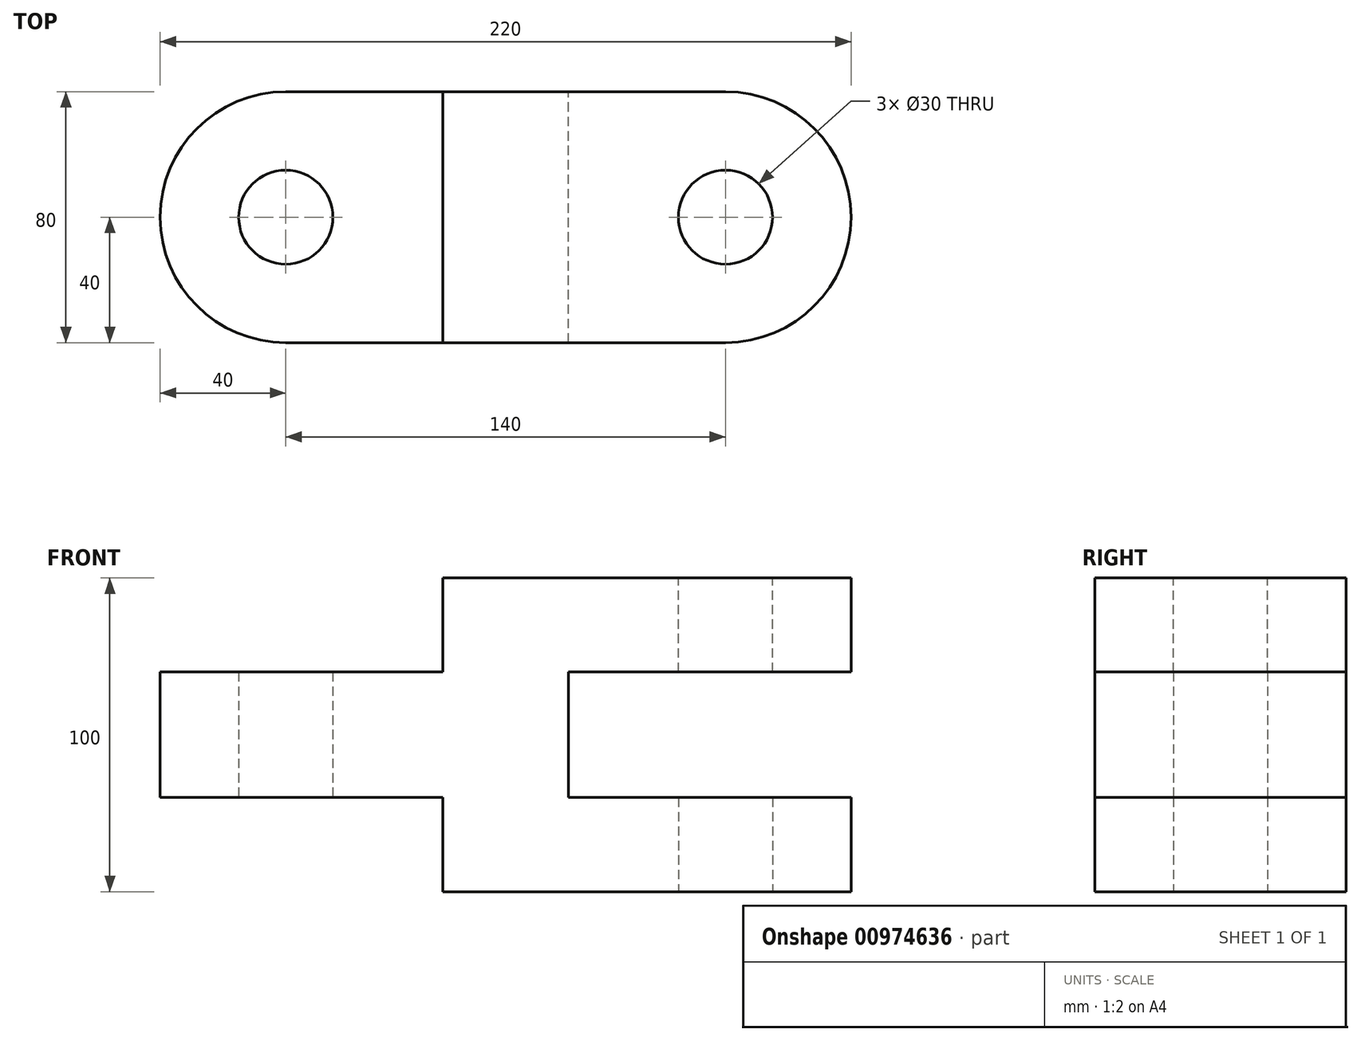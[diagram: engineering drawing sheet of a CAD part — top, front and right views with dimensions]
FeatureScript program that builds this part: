
annotation { "Feature Type Name" : "Feature", "Feature Type Description" : "" }
export const myFeature = defineFeature(function(context is Context, id is Id, definition is map)
    precondition{}
    {
        {
            var Q0;
            Q0=qCreatedBy(makeId("Front.planeOp"),FACE);
            var sketch = newSketch(context, id + "F0", { "sketchPlane" : qUnion([Q0])});
            skLineSegment(sketch, "E0.bottom", {"start": v(0, 0) * mm, "end": v(-40, 0) * mm});
            skLineSegment(sketch, "E0.top", {"start": v(0, 100) * mm, "end": v(-40, 100) * mm});
            skLineSegment(sketch, "E0.left", {"start": v(0, 0) * mm, "end": v(0, 100) * mm});
            skLineSegment(sketch, "E0.right", {"start": v(-40, 0) * mm, "end": v(-40, 100) * mm});
            skLineSegment(sketch, "E1.bottom", {"start": v(0, 0) * mm, "end": v(50, 0) * mm});
            skLineSegment(sketch, "E1.top", {"start": v(0, 30) * mm, "end": v(50, 30) * mm});
            skLineSegment(sketch, "E1.left", {"start": v(0, 0) * mm, "end": v(0, 30) * mm});
            skLineSegment(sketch, "E1.right", {"start": v(50, 0) * mm, "end": v(50, 30) * mm});
            skLineSegment(sketch, "E2.bottom", {"start": v(0, 100) * mm, "end": v(50, 100) * mm});
            skLineSegment(sketch, "E2.top", {"start": v(0, 70) * mm, "end": v(50, 70) * mm});
            skLineSegment(sketch, "E2.left", {"start": v(0, 100) * mm, "end": v(0, 70) * mm});
            skLineSegment(sketch, "E2.right", {"start": v(50, 100) * mm, "end": v(50, 70) * mm});
            skLineSegment(sketch, "E3.bottom", {"start": v(-90, 70) * mm, "end": v(-40, 70) * mm});
            skLineSegment(sketch, "E3.top", {"start": v(-90, 30) * mm, "end": v(-40, 30) * mm});
            skLineSegment(sketch, "E3.left", {"start": v(-90, 70) * mm, "end": v(-90, 30) * mm});
            skLineSegment(sketch, "E3.right", {"start": v(-40, 70) * mm, "end": v(-40, 30) * mm});
            skSolve(sketch);
        }
        {
            var Q0;
            Q0=makeQuery(id+"F0.imprint","IMPRINT",FACE,{"disambiguationData":[TD([[makeQuery(id+"F0.imprint","IMPRINT",EDGE,{"derivedFrom":sQuery(id+"F0.wireOp",EDGE,"E1.bottom")}),1.0]])]});
            var Q1;
            {var subQ1=sQuery(id+"F0.wireOp",EDGE,"E0.bottom");Q1=makeQuery(id+"F0.imprint","IMPRINT",FACE,{"disambiguationData":[TD([[makeQuery(id+"F0.imprint","IMPRINT",EDGE,{"derivedFrom":subQ1}),-1.0]])]});}
            var Q2;
            Q2=makeQuery(id+"F0.imprint","IMPRINT",FACE,{"disambiguationData":[TD([[makeQuery(id+"F0.imprint","IMPRINT",EDGE,{"derivedFrom":sQuery(id+"F0.wireOp",EDGE,"E2.bottom")}),-1.0]])]});
            var Q3;
            Q3=makeQuery(id+"F0.imprint","IMPRINT",FACE,{"disambiguationData":[TD([[makeQuery(id+"F0.imprint","IMPRINT",EDGE,{"derivedFrom":sQuery(id+"F0.wireOp",EDGE,"E3.bottom")}),-1.0]])]});
            extrude(context, id + "F1", {"entities" : qUnion([Q0, Q1, Q2, Q3]), "depth" : 80 * mm, "offsetDistance" : 25 * mm});
        }
        {
            var Q0;
            Q0=makeQuery(id+"F1.opExtrude","SWEPT_FACE",FACE,{"disambiguationData":[OSD([sQuery(id+"F0.wireOp",EDGE,"E0.top"),sQuery(id+"F0.wireOp",EDGE,"E2.bottom")])]});
            var sketch = newSketch(context, id + "F2", { "sketchPlane" : qUnion([Q0])});
            skPoint(sketch, "E4", {"position": v(50, -40) * mm});
            skCircle(sketch, "E5", {"center": v(50, -40) * mm, "radius": 40 * mm});
            skCircle(sketch, "E6", {"center": v(50, -40) * mm, "radius": 15 * mm});
            skSolve(sketch);
        }
        {
            var Q0;
            Q0=makeQuery(id+"F1.opExtrude","SWEPT_FACE",FACE,{"disambiguationData":[OSD([sQuery(id+"F0.wireOp",EDGE,"E0.bottom"),sQuery(id+"F0.wireOp",EDGE,"E1.bottom")])]});
            var sketch = newSketch(context, id + "F3", { "sketchPlane" : qUnion([Q0])});
            skPoint(sketch, "E7", {"position": v(50, 40) * mm});
            skCircle(sketch, "E8", {"center": v(50, 40) * mm, "radius": 40 * mm});
            skCircle(sketch, "E9", {"center": v(50, 40) * mm, "radius": 15 * mm});
            skSolve(sketch);
        }
        {
            var Q0;
            Q0=makeQuery(id+"F1.opExtrude","SWEPT_FACE",FACE,{"disambiguationData":[OSD([sQuery(id+"F0.wireOp",EDGE,"E3.top")])]});
            var sketch = newSketch(context, id + "F4", { "sketchPlane" : qUnion([Q0])});
            skPoint(sketch, "E10", {"position": v(-90, 40) * mm});
            skCircle(sketch, "E11", {"center": v(-90, 40) * mm, "radius": 40 * mm});
            skCircle(sketch, "E12", {"center": v(-90, 40) * mm, "radius": 15 * mm});
            skSolve(sketch);
        }
        {
            var Q0;
            Q0 = qSketchRegion(id + "F2", true);
            var Q1;
            Q1=makeQuery(id+"F1.opExtrude","SWEPT_FACE",FACE,{"disambiguationData":[OSD([sQuery(id+"F0.wireOp",EDGE,"E2.top")])]});
            extrude(context, id + "F5", {"entities" : qUnion([Q0]), "operationType" : NewBodyOperationType.ADD, "endBound" : BoundingType.UP_TO_SURFACE, "oppositeDirection" : true, "depth" : 25 * mm, "endBoundEntityFace" : qUnion([Q1]), "offsetDistance" : 25 * mm});
        }
        {
            var Q0;
            {var subQ0=sQuery(id+"F2.wireOp",EDGE,"E6");var subQ1=makeQuery(id+"F1.opExtrude","SWEPT_EDGE",EDGE,{"disambiguationData":[OSD([sQuery(id+"F0.wireOp",EDGE,"E2.bottom"),sQuery(id+"F0.wireOp",EDGE,"E2.right")])]});var subQ2=makeQuery(id+"F2.imprint","INTERSECT",VERTEX,{"disambiguationData":[OD(0.0)],"derivedFrom":[subQ1,subQ0]});Q0=makeQuery(id+"F2.imprint","IMPRINT",FACE,{"disambiguationData":[TD([[makeQuery(id+"F2.imprint","IMPRINT",EDGE,{"disambiguationData":[TD([[subQ2,-1.0]])],"derivedFrom":subQ0}),1.0]])]});}
            extrude(context, id + "F6", {"entities" : qUnion([Q0]), "operationType" : NewBodyOperationType.REMOVE, "oppositeDirection" : true, "depth" : 30 * mm, "offsetDistance" : 25 * mm});
        }
        {
            var Q0;
            {var subQ1=sQuery(id+"F0.wireOp",EDGE,"E1.bottom");var subQ3=makeQuery(id+"F1.opExtrude","SWEPT_EDGE",EDGE,{"disambiguationData":[OSD([subQ1,sQuery(id+"F0.wireOp",EDGE,"E1.right")])]});var subQ6=sQuery(id+"F3.wireOp",EDGE,"E9");var subQ7=makeQuery(id+"F3.imprint","INTERSECT",VERTEX,{"disambiguationData":[OD(0.0)],"derivedFrom":[subQ3,subQ6]});Q0=makeQuery(id+"F3.imprint","IMPRINT",FACE,{"disambiguationData":[TD([[makeQuery(id+"F3.imprint","IMPRINT",EDGE,{"disambiguationData":[TD([[subQ7,-1.0]])],"derivedFrom":subQ6}),-1.0]])]});}
            var Q1;
            Q1=makeQuery(id+"F1.opExtrude","SWEPT_FACE",FACE,{"disambiguationData":[OSD([sQuery(id+"F0.wireOp",EDGE,"E1.top")])]});
            extrude(context, id + "F7", {"entities" : qUnion([Q0]), "operationType" : NewBodyOperationType.ADD, "endBound" : BoundingType.UP_TO_SURFACE, "oppositeDirection" : true, "depth" : 25 * mm, "endBoundEntityFace" : qUnion([Q1]), "offsetDistance" : 25 * mm});
        }
        {
            var Q0;
            {var subQ0=sQuery(id+"F3.wireOp",EDGE,"E9");var subQ1=makeQuery(id+"F1.opExtrude","SWEPT_EDGE",EDGE,{"disambiguationData":[OSD([sQuery(id+"F0.wireOp",EDGE,"E1.bottom"),sQuery(id+"F0.wireOp",EDGE,"E1.right")])]});var subQ2=makeQuery(id+"F3.imprint","INTERSECT",VERTEX,{"disambiguationData":[OD(0.0)],"derivedFrom":[subQ1,subQ0]});Q0=makeQuery(id+"F3.imprint","IMPRINT",FACE,{"disambiguationData":[TD([[makeQuery(id+"F3.imprint","IMPRINT",EDGE,{"disambiguationData":[TD([[subQ2,1.0]])],"derivedFrom":subQ0}),1.0]])]});}
            extrude(context, id + "F8", {"entities" : qUnion([Q0]), "operationType" : NewBodyOperationType.REMOVE, "oppositeDirection" : true, "depth" : 30 * mm, "offsetDistance" : 25 * mm});
        }
        {
            var Q0;
            {var subQ1=sQuery(id+"F0.wireOp",EDGE,"E3.top");var subQ2=makeQuery(id+"F1.opExtrude","SWEPT_EDGE",EDGE,{"disambiguationData":[OSD([subQ1,sQuery(id+"F0.wireOp",EDGE,"E3.left")])]});var subQ5=sQuery(id+"F4.wireOp",EDGE,"E12");var subQ6=makeQuery(id+"F4.imprint","INTERSECT",VERTEX,{"disambiguationData":[OD(0.0)],"derivedFrom":[subQ2,subQ5]});Q0=makeQuery(id+"F4.imprint","IMPRINT",FACE,{"disambiguationData":[TD([[makeQuery(id+"F4.imprint","IMPRINT",EDGE,{"disambiguationData":[TD([[subQ6,1.0]])],"derivedFrom":subQ5}),-1.0]])]});}
            var Q1;
            Q1=makeQuery(id+"F1.opExtrude","SWEPT_FACE",FACE,{"disambiguationData":[OSD([sQuery(id+"F0.wireOp",EDGE,"E3.bottom")])]});
            extrude(context, id + "F9", {"entities" : qUnion([Q0]), "operationType" : NewBodyOperationType.ADD, "endBound" : BoundingType.UP_TO_SURFACE, "oppositeDirection" : true, "depth" : 25 * mm, "endBoundEntityFace" : qUnion([Q1]), "offsetDistance" : 25 * mm});
        }
        {
            var Q0;
            {var subQ0=sQuery(id+"F4.wireOp",EDGE,"E12");var subQ1=makeQuery(id+"F1.opExtrude","SWEPT_EDGE",EDGE,{"disambiguationData":[OSD([sQuery(id+"F0.wireOp",EDGE,"E3.top"),sQuery(id+"F0.wireOp",EDGE,"E3.left")])]});var subQ2=makeQuery(id+"F4.imprint","INTERSECT",VERTEX,{"disambiguationData":[OD(0.0)],"derivedFrom":[subQ1,subQ0]});Q0=makeQuery(id+"F4.imprint","IMPRINT",FACE,{"disambiguationData":[TD([[makeQuery(id+"F4.imprint","IMPRINT",EDGE,{"disambiguationData":[TD([[subQ2,-1.0]])],"derivedFrom":subQ0}),1.0]])]});}
            extrude(context, id + "F10", {"entities" : qUnion([Q0]), "operationType" : NewBodyOperationType.REMOVE, "oppositeDirection" : true, "depth" : 40 * mm, "offsetDistance" : 25 * mm});
        }
    });
